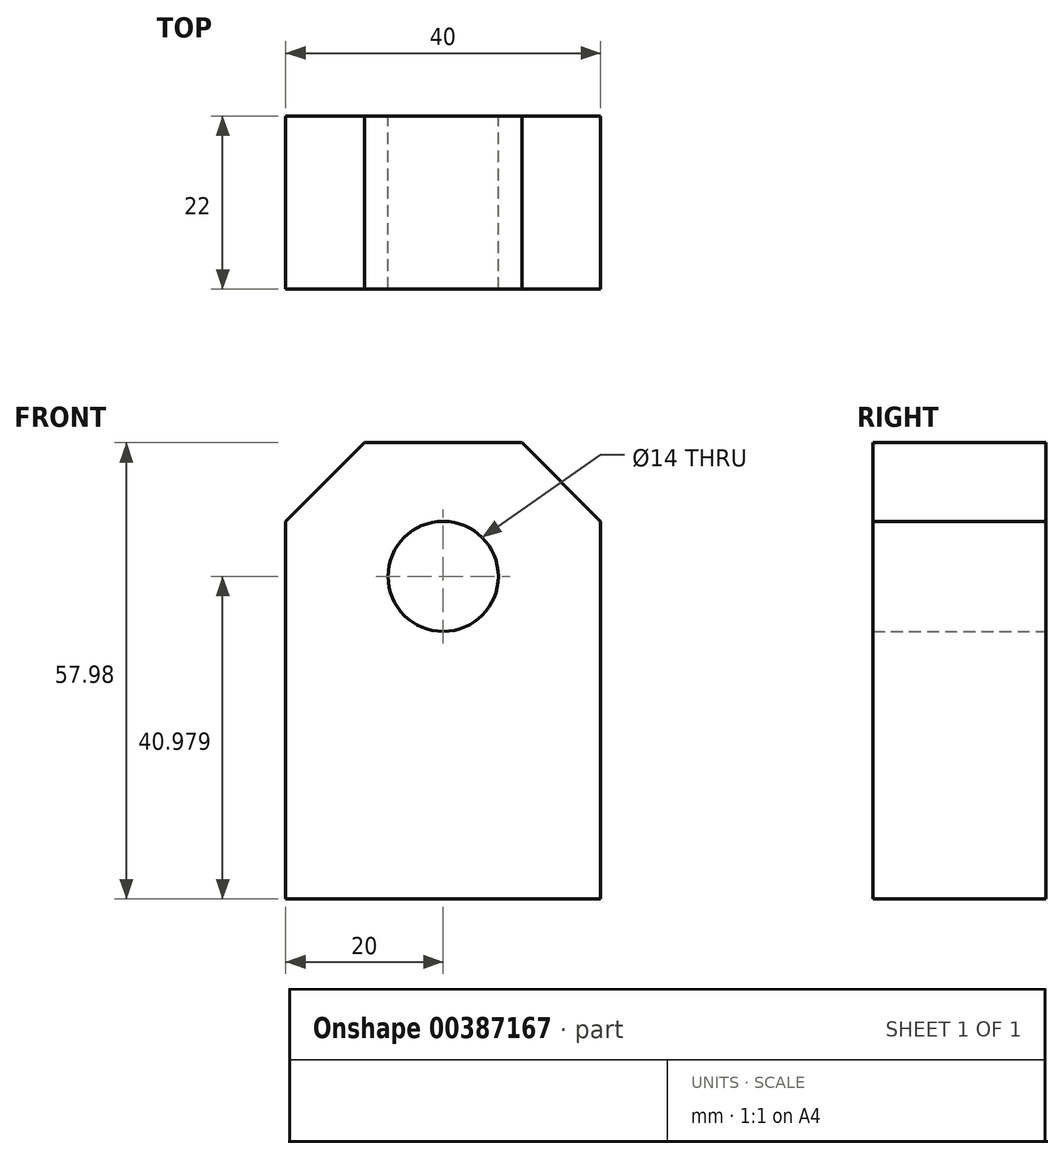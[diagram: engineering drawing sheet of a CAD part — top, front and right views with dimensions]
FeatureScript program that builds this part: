
annotation { "Feature Type Name" : "Feature", "Feature Type Description" : "" }
export const myFeature = defineFeature(function(context is Context, id is Id, definition is map)
    precondition{}
    {
        {
            var Q0;
            Q0=qCreatedBy(makeId("Front.planeOp"),FACE);
            var sketch = newSketch(context, id + "F0", { "sketchPlane" : qUnion([Q0])});
            skLineSegment(sketch, "E0", {"start": v(0, 0) * mm, "end": v(20, 0) * mm});
            skLineSegment(sketch, "E1", {"start": v(0, 0) * mm, "end": v(-20, 0) * mm});
            skLineSegment(sketch, "E2", {"start": v(0, 0) * mm, "end": v(0, 29) * mm});
            skLineSegment(sketch, "E3", {"start": v(0, 0) * mm, "end": v(0, -29) * mm});
            skLineSegment(sketch, "E4", {"start": v(0, -29) * mm, "end": v(20, -29) * mm});
            skLineSegment(sketch, "E5", {"start": v(20, -29) * mm, "end": v(20, 0) * mm});
            skLineSegment(sketch, "E6", {"start": v(0, 29) * mm, "end": v(20, 29) * mm});
            skLineSegment(sketch, "E7", {"start": v(20, 29) * mm, "end": v(20, 0) * mm});
            skLineSegment(sketch, "E8", {"start": v(0, 29) * mm, "end": v(-20, 29) * mm});
            skLineSegment(sketch, "E9", {"start": v(-20, 29) * mm, "end": v(-20, 0) * mm});
            skLineSegment(sketch, "E10", {"start": v(-20, 0) * mm, "end": v(-20, -29) * mm});
            skLineSegment(sketch, "E11", {"start": v(-20, -29) * mm, "end": v(0, -29) * mm});
            skLineSegment(sketch, "E12", {"start": v(0, 29) * mm, "end": v(0, 18.99) * mm});
            skCircle(sketch, "E13", {"center": v(0, 11.99) * mm, "radius": 7 * mm});
            skSolve(sketch);
        }
        {
            var Q0;
            Q0=makeQuery(id+"F0.imprint","IMPRINT",FACE,{"disambiguationData":[TD([[makeQuery(id+"F0.imprint","IMPRINT",EDGE,{"derivedFrom":sQuery(id+"F0.wireOp",EDGE,"E0")}),-1.0]])]});
            var Q1;
            {var subQ1=sQuery(id+"F0.wireOp",EDGE,"E0");Q1=makeQuery(id+"F0.imprint","IMPRINT",FACE,{"disambiguationData":[TD([[makeQuery(id+"F0.imprint","IMPRINT",EDGE,{"derivedFrom":subQ1}),1.0]])]});}
            var Q2;
            {var subQ1=sQuery(id+"F0.wireOp",EDGE,"E1");Q2=makeQuery(id+"F0.imprint","IMPRINT",FACE,{"disambiguationData":[TD([[makeQuery(id+"F0.imprint","IMPRINT",EDGE,{"derivedFrom":subQ1}),-1.0]])]});}
            var Q3;
            Q3=makeQuery(id+"F0.imprint","IMPRINT",FACE,{"disambiguationData":[TD([[makeQuery(id+"F0.imprint","IMPRINT",EDGE,{"derivedFrom":sQuery(id+"F0.wireOp",EDGE,"E1")}),1.0]])]});
            extrude(context, id + "F1", {"entities" : qUnion([Q0, Q1, Q2, Q3]), "depth" : 22 * mm});
        }
        {
            var Q0;
            Q0=makeQuery(id+"F1.opExtrude","SWEPT_EDGE",EDGE,{"disambiguationData":[OSD([sQuery(id+"F0.wireOp",EDGE,"E6"),sQuery(id+"F0.wireOp",EDGE,"E7")])]});
            var Q1;
            Q1=makeQuery(id+"F1.opExtrude","SWEPT_EDGE",EDGE,{"disambiguationData":[OSD([sQuery(id+"F0.wireOp",EDGE,"E8"),sQuery(id+"F0.wireOp",EDGE,"E9")])]});
            chamfer(context, id + "F2", {"entities" : qUnion([Q0, Q1]), "width" : 10 * mm, "tangentPropagation" : true});
        }
    });
